# Revit family: BSHH
name_source: partatom
category: Air Terminals
revit_build: Autodesk Revit MEP 2012 (Build: 20110309_2315(x64)
units: mm (PartAtom-declared; Revit-internal decimal feet)

## types (4) — shared parameters
Manufacturer = INNE
Máxima presión estática = 0.00 in-wg
Máxima velocidad de cuello = 0 FPM
Mínima presión estática = 0.00 in-wg
Mínima velocidad de cuello = 0 FPM
Travesaño medio = Yes
Travesaños laterales = No
URL = http://www.inne.com.mx
separación = 3/4"

## per-type parameters (varying)
| type | A Largo | Altura | B Alto | B marco | Height | N° de rejillas | Width |
| BSHH-20-12 | 19 13/32" | 1 1/2" | 11 13/32" | 12 29/32" | 12 29/32" | 15 | 20 29/32" |
| BSHH-21-13 | 20 13/32" | 1 7/8" | 12 13/32" | 13 29/32" | 13 29/32" | 17 | 21 29/32" |
| BSHH-22-14 | 21 13/32" | 1 7/8" | 13 13/32" | 14 29/32" | 14 29/32" | 18 | 22 29/32" |
| BSHH-23-15 | 22 13/32" | 1 7/8" | 14 13/32" | 15 29/32" | 15 29/32" | 19 | 23 29/32" |

## geometry (parser evidence)
native form markers: Sweep x5
no freeform markers — native parametric forms only
